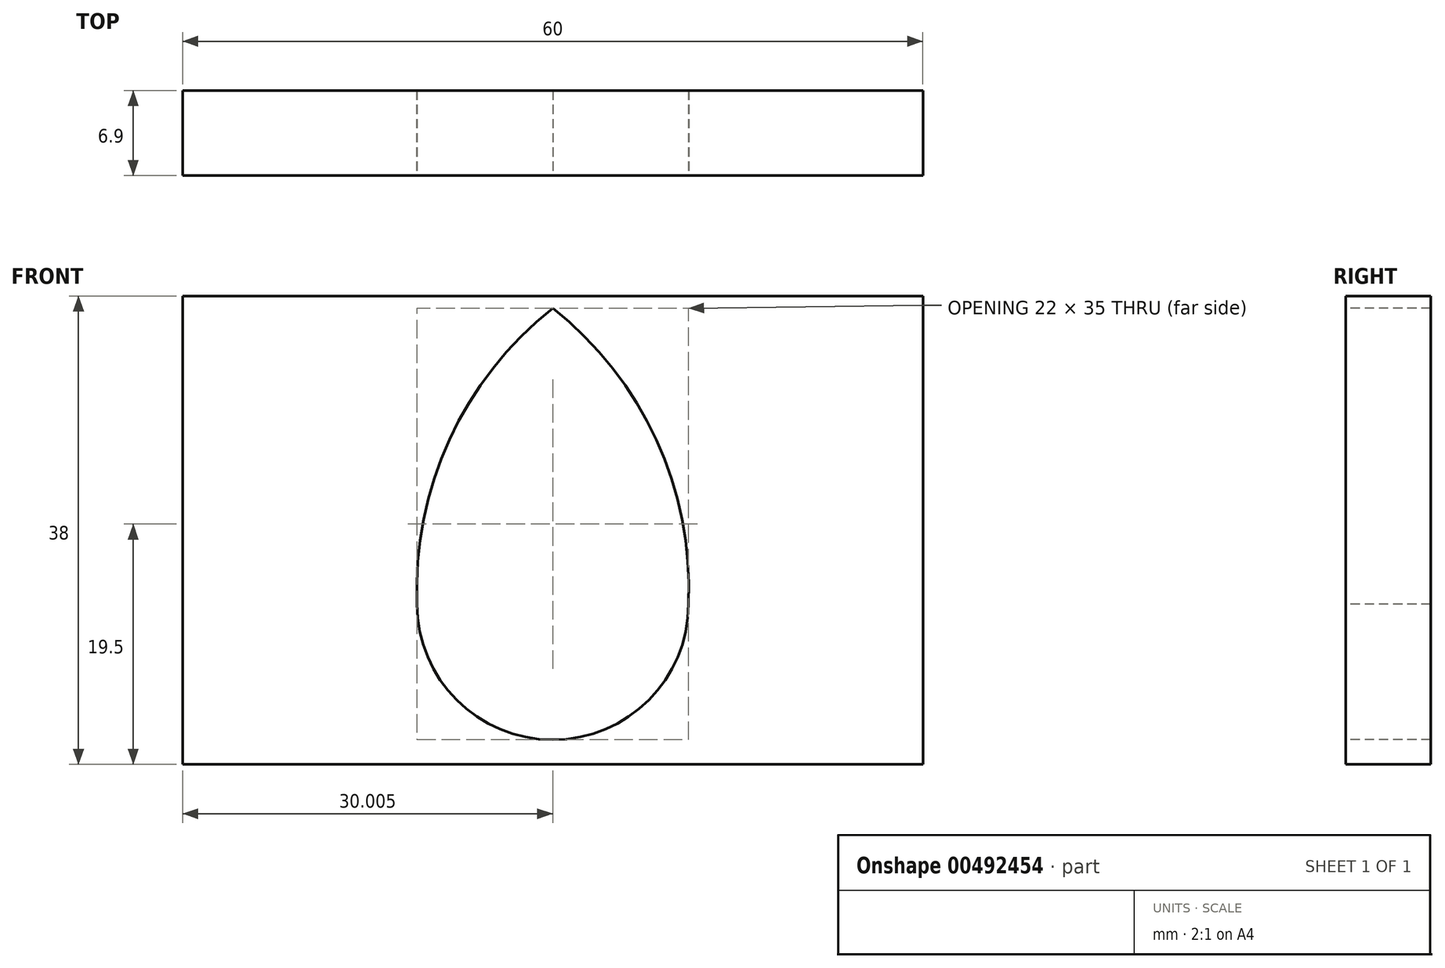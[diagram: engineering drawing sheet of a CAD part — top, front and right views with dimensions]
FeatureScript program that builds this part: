
annotation { "Feature Type Name" : "Feature", "Feature Type Description" : "" }
export const myFeature = defineFeature(function(context is Context, id is Id, definition is map)
    precondition{}
    {
        {
            var Q0;
            Q0=qCreatedBy(makeId("Top.planeOp"),FACE);
            var sketch = newSketch(context, id + "F0", { "sketchPlane" : qUnion([Q0])});
            skLineSegment(sketch, "E0.bottom", {"start": v(-35.2, 14.25) * mm, "end": v(24.8, 14.25) * mm});
            skLineSegment(sketch, "E0.top", {"start": v(-35.2, 7.35) * mm, "end": v(24.8, 7.35) * mm});
            skLineSegment(sketch, "E0.left", {"start": v(-35.2, 14.25) * mm, "end": v(-35.2, 7.35) * mm});
            skLineSegment(sketch, "E0.right", {"start": v(24.8, 14.25) * mm, "end": v(24.8, 7.35) * mm});
            skSolve(sketch);
        }
        {
            var Q0;
            Q0 = qSketchRegion(id + "F0", true);
            extrude(context, id + "F1", {"entities" : qUnion([Q0]), "depth" : 38 * mm});
        }
        {
            var Q0;
            Q0=makeQuery(id+"F1.opExtrude","SWEPT_FACE",FACE,{"disambiguationData":[OSD([sQuery(id+"F0.wireOp",EDGE,"E0.top")])]});
            var sketch = newSketch(context, id + "F2", { "sketchPlane" : qUnion([Q0])});
            skArc(sketch, "E1", {"start": v(-16.2, 13) * mm, "mid": v(-5.2, 2) * mm, "end": v(5.8, 13) * mm});
            skPoint(sketch, "E2", {"position": v(-5.2, 37) * mm});
            skArc(sketch, "E3", {"start": v(5.8, 13) * mm, "mid": v(3.2, 26.32) * mm, "end": v(-5.2, 37) * mm});
            skLineSegment(sketch, "E4", {"start": v(-5.2, 46.48) * mm, "end": v(-5.2, -11.21) * mm, "construction": true});
            skPoint(sketch, "E4.startSnap0", {"position": v(-5.2, 38) * mm});
            skArc(sketch, "E5.MirrorCS", {"start": v(-16.2, 13) * mm, "mid": v(-13.58, 26.32) * mm, "end": v(-5.2, 37) * mm});
            skSolve(sketch);
        }
        {
            var Q0;
            {var subQ1=sQuery(id+"F2.wireOp",EDGE,"E1");var subQ4=sQuery(id+"F2.wireOp",EDGE,"E3");var subQ7=makeQuery(id+"F2.imprint","INTERSECT",VERTEX,{"disambiguationData":[OD(1.0)],"derivedFrom":[subQ1,subQ4]});Q0=makeQuery(id+"F2.imprint","IMPRINT",FACE,{"disambiguationData":[TD([[makeQuery(id+"F2.imprint","IMPRINT",EDGE,{"disambiguationData":[TD([[subQ7,1.0]])],"derivedFrom":subQ1}),1.0]])]});}
            extrude(context, id + "F3", {"entities" : qUnion([Q0]), "operationType" : NewBodyOperationType.REMOVE, "oppositeDirection" : true, "depth" : 25 * mm});
        }
    });
